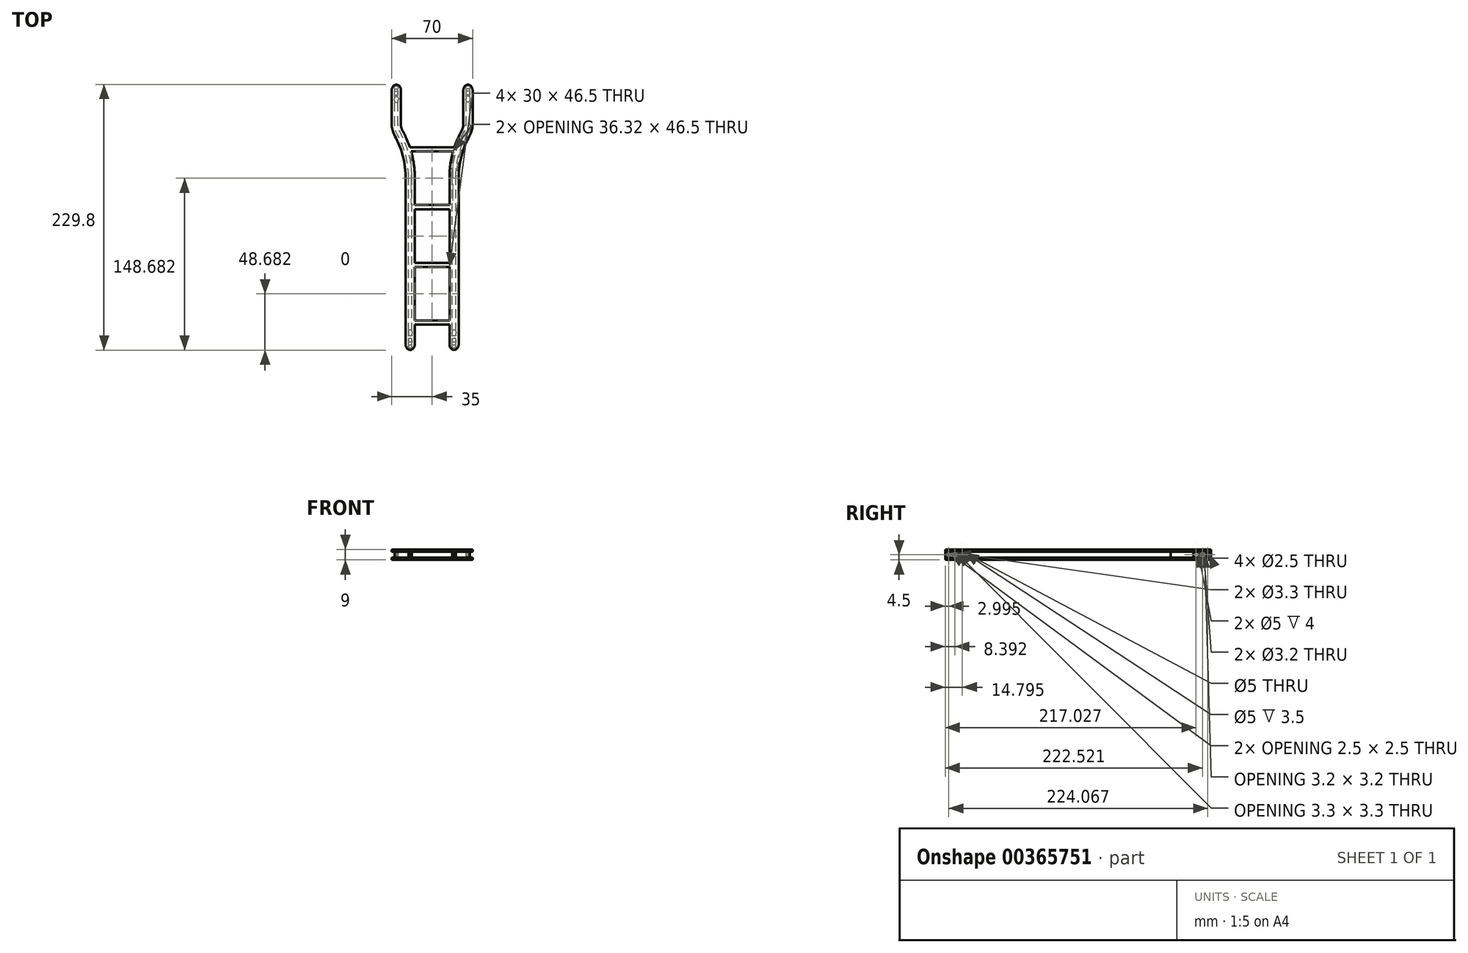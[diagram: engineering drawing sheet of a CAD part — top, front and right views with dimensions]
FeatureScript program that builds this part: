
annotation { "Feature Type Name" : "Feature", "Feature Type Description" : "" }
export const myFeature = defineFeature(function(context is Context, id is Id, definition is map)
    precondition{}
    {
        {
            var Q0;
            Q0=qCreatedBy(makeId("Front.planeOp"),FACE);
            var sketch = newSketch(context, id + "F0", { "sketchPlane" : qUnion([Q0])});
            skLineSegment(sketch, "E0.bottom", {"start": v(-15, 0) * mm, "end": v(-23, 0) * mm});
            skLineSegment(sketch, "E0.top", {"start": v(-15, 9) * mm, "end": v(-23, 9) * mm});
            skLineSegment(sketch, "E0.left", {"start": v(-15, 0) * mm, "end": v(-15, 2) * mm});
            skLineSegment(sketch, "E0.right", {"start": v(-23, 0) * mm, "end": v(-23, 2) * mm});
            skLineSegment(sketch, "E1.bottom", {"start": v(-23, 7) * mm, "end": v(-21, 7) * mm});
            skLineSegment(sketch, "E1.top", {"start": v(-23, 2) * mm, "end": v(-21, 2) * mm});
            skLineSegment(sketch, "E1.right", {"start": v(-20.5, 6.5) * mm, "end": v(-20.5, 2.5) * mm});
            skLineSegment(sketch, "E2.bottom", {"start": v(-17, 7) * mm, "end": v(-15, 7) * mm});
            skLineSegment(sketch, "E2.top", {"start": v(-17, 2) * mm, "end": v(-15, 2) * mm});
            skLineSegment(sketch, "E2.left", {"start": v(-17.5, 6.5) * mm, "end": v(-17.5, 2.5) * mm});
            skLineSegment(sketch, "E3", {"start": v(-19, 9) * mm, "end": v(-19, -4.59) * mm, "construction": true});
            skPoint(sketch, "E3.endSnap0", {"position": v(-19, 0) * mm});
            skLineSegment(sketch, "E4.trimOffspring", {"start": v(-15, 7) * mm, "end": v(-15, 9) * mm});
            skLineSegment(sketch, "E5.trimOffspring", {"start": v(-23, 7) * mm, "end": v(-23, 9) * mm});
            skPoint(sketch, "E6.visualSharp", {"position": v(-20.5, 7) * mm});
            skArc(sketch, "E6.filletArc", {"start": v(-20.5, 6.5) * mm, "mid": v(-20.65, 6.85) * mm, "end": v(-21, 7) * mm});
            skPoint(sketch, "E7.visualSharp", {"position": v(-17.5, 7) * mm});
            skArc(sketch, "E7.filletArc", {"start": v(-17, 7) * mm, "mid": v(-17.35, 6.85) * mm, "end": v(-17.5, 6.5) * mm});
            skPoint(sketch, "E8.visualSharp", {"position": v(-17.5, 2) * mm});
            skArc(sketch, "E8.filletArc", {"start": v(-17.5, 2.5) * mm, "mid": v(-17.35, 2.15) * mm, "end": v(-17, 2) * mm});
            skPoint(sketch, "E9.visualSharp", {"position": v(-20.5, 2) * mm});
            skArc(sketch, "E9.filletArc", {"start": v(-21, 2) * mm, "mid": v(-20.65, 2.15) * mm, "end": v(-20.5, 2.5) * mm});
            skSolve(sketch);
        }
        {
            var Q0;
            Q0=qCreatedBy(makeId("Top.planeOp"),FACE);
            var sketch = newSketch(context, id + "F1", { "sketchPlane" : qUnion([Q0])});
            skLineSegment(sketch, "E10", {"start": v(-35.26, 0) * mm, "end": v(-35.26, 150) * mm});
            skLineSegment(sketch, "E11", {"start": v(-47.26, 230) * mm, "end": v(-47.26, 195) * mm});
            skFitSpline(sketch, "E12", {"points": [v(-35.26, 150) * mm, v(-40.7, 174.86) * mm, v(-47.26, 195) * mm], "startDerivative": vector(-0.38, 53.31) * mm, "endDerivative": vector(-0.87, 58.08) * mm});
            skSolve(sketch);
        }
        {
            var Q0;
            Q0 = qSketchRegion(id + "F0", true);
            var Q1;
            Q1 = qConstructionFilter(qBodyType(qCreatedBy(id + "F1" ,EDGE), BodyType.WIRE), ConstructionObject.NO);
            sweep(context, id + "F2", {"profiles" : qUnion([Q0]), "path" : qUnion([Q1])});
        }
        {
            var Q0;
            Q0=makeQuery(id+"F2.opSweep","SWEPT_FACE",FACE,{"disambiguationData":[OSD([sQuery(id+"F0.wireOp",EDGE,"E4.trimOffspring"),sQuery(id+"F1.wireOp",EDGE,"E10")])]});
            var sketch = newSketch(context, id + "F3", { "sketchPlane" : qUnion([Q0])});
            skLineSegment(sketch, "E13.bottom", {"start": v(22.03, 9) * mm, "end": v(25.53, 9) * mm});
            skLineSegment(sketch, "E13.top", {"start": v(22.03, 7) * mm, "end": v(25.53, 7) * mm});
            skLineSegment(sketch, "E13.left", {"start": v(22.03, 9) * mm, "end": v(22.03, 7) * mm});
            skLineSegment(sketch, "E13.right", {"start": v(25.53, 9) * mm, "end": v(25.53, 7) * mm});
            skLineSegment(sketch, "E14.0.1.0", {"start": v(22.03, 2) * mm, "end": v(22.03, 0) * mm});
            skLineSegment(sketch, "E14.0.1.1", {"start": v(22.03, 0) * mm, "end": v(25.53, 0) * mm});
            skLineSegment(sketch, "E14.0.1.2", {"start": v(22.03, 2) * mm, "end": v(25.53, 2) * mm});
            skLineSegment(sketch, "E14.0.1.3", {"start": v(25.53, 2) * mm, "end": v(25.53, 0) * mm});
            skLineSegment(sketch, "E14.1.0.0", {"start": v(72.03, 9) * mm, "end": v(72.03, 7) * mm});
            skLineSegment(sketch, "E14.1.0.1", {"start": v(72.03, 7) * mm, "end": v(75.53, 7) * mm});
            skLineSegment(sketch, "E14.1.0.2", {"start": v(72.03, 9) * mm, "end": v(75.53, 9) * mm});
            skLineSegment(sketch, "E14.1.0.3", {"start": v(75.53, 9) * mm, "end": v(75.53, 7) * mm});
            skLineSegment(sketch, "E14.1.1.0", {"start": v(72.03, 2) * mm, "end": v(72.03, 0) * mm});
            skLineSegment(sketch, "E14.1.1.1", {"start": v(72.03, 0) * mm, "end": v(75.53, 0) * mm});
            skLineSegment(sketch, "E14.1.1.2", {"start": v(72.03, 2) * mm, "end": v(75.53, 2) * mm});
            skLineSegment(sketch, "E14.1.1.3", {"start": v(75.53, 2) * mm, "end": v(75.53, 0) * mm});
            skLineSegment(sketch, "E14.2.0.0", {"start": v(122.03, 9) * mm, "end": v(122.03, 7) * mm});
            skLineSegment(sketch, "E14.2.0.1", {"start": v(122.03, 7) * mm, "end": v(125.53, 7) * mm});
            skLineSegment(sketch, "E14.2.0.2", {"start": v(122.03, 9) * mm, "end": v(125.53, 9) * mm});
            skLineSegment(sketch, "E14.2.0.3", {"start": v(125.53, 9) * mm, "end": v(125.53, 7) * mm});
            skLineSegment(sketch, "E14.2.1.0", {"start": v(122.03, 2) * mm, "end": v(122.03, 0) * mm});
            skLineSegment(sketch, "E14.2.1.1", {"start": v(122.03, 0) * mm, "end": v(125.53, 0) * mm});
            skLineSegment(sketch, "E14.2.1.2", {"start": v(122.03, 2) * mm, "end": v(125.53, 2) * mm});
            skLineSegment(sketch, "E14.2.1.3", {"start": v(125.53, 2) * mm, "end": v(125.53, 0) * mm});
            skLineSegment(sketch, "E14.3.0.0", {"start": v(172.03, 9) * mm, "end": v(172.03, 7) * mm});
            skLineSegment(sketch, "E14.3.0.1", {"start": v(172.03, 7) * mm, "end": v(175.53, 7) * mm});
            skLineSegment(sketch, "E14.3.0.2", {"start": v(172.03, 9) * mm, "end": v(175.53, 9) * mm});
            skLineSegment(sketch, "E14.3.0.3", {"start": v(175.53, 9) * mm, "end": v(175.53, 7) * mm});
            skLineSegment(sketch, "E14.3.1.0", {"start": v(172.03, 2) * mm, "end": v(172.03, 0) * mm});
            skLineSegment(sketch, "E14.3.1.1", {"start": v(172.03, 0) * mm, "end": v(175.53, 0) * mm});
            skLineSegment(sketch, "E14.3.1.2", {"start": v(172.03, 2) * mm, "end": v(175.53, 2) * mm});
            skLineSegment(sketch, "E14.3.1.3", {"start": v(175.53, 2) * mm, "end": v(175.53, 0) * mm});
            skLineSegment(sketch, "E14.direction1", {"start": v(22.03, 7) * mm, "end": v(72.03, 7) * mm, "construction": true});
            skLineSegment(sketch, "E14.direction2", {"start": v(22.03, 7) * mm, "end": v(22.03, 0) * mm, "construction": true});
            skSolve(sketch);
        }
        {
            var Q0;
            Q0 = qSketchRegion(id + "F3", true);
            extrude(context, id + "F4", {"entities" : qUnion([Q0]), "operationType" : NewBodyOperationType.ADD, "depth" : 15 * mm});
        }
        {
            var Q0;
            Q0=makeQuery(id+"F4.opExtrude","CAP_FACE",FACE,{"disambiguationData":[OSD([sQuery(id+"F3.wireOp",EDGE,"E14.3.0.0"),sQuery(id+"F3.wireOp",EDGE,"E14.3.0.1"),sQuery(id+"F3.wireOp",EDGE,"E14.3.0.2"),sQuery(id+"F3.wireOp",EDGE,"E14.3.0.3")])],"isStart":true});
            var sketch = newSketch(context, id + "F5", { "sketchPlane" : qUnion([Q0])});
            skLineSegment(sketch, "E15.0", {"start": v(-172.03, 7) * mm, "end": v(-175.53, 7) * mm});
            skLineSegment(sketch, "E16.0.0", {"start": v(-175.53, 9) * mm, "end": v(-175.53, 7) * mm});
            skLineSegment(sketch, "E16.0.1", {"start": v(-175.53, 7) * mm, "end": v(-172.03, 7) * mm});
            skLineSegment(sketch, "E16.0.2", {"start": v(-172.03, 7) * mm, "end": v(-172.03, 9) * mm});
            skLineSegment(sketch, "E16.0.3", {"start": v(-172.03, 9) * mm, "end": v(-175.53, 9) * mm});
            skLineSegment(sketch, "E17.0.0", {"start": v(-175.53, 2) * mm, "end": v(-175.53, 0) * mm});
            skLineSegment(sketch, "E17.0.1", {"start": v(-175.53, 0) * mm, "end": v(-172.03, 0) * mm});
            skLineSegment(sketch, "E17.0.2", {"start": v(-172.03, 0) * mm, "end": v(-172.03, 2) * mm});
            skLineSegment(sketch, "E17.0.3", {"start": v(-172.03, 2) * mm, "end": v(-175.53, 2) * mm});
            skSolve(sketch);
        }
        {
            var Q0;
            Q0 = qSketchRegion(id + "F5", true);
            extrude(context, id + "F6", {"entities" : qUnion([Q0]), "operationType" : NewBodyOperationType.ADD, "endBound" : BoundingType.UP_TO_NEXT, "depth" : 25 * mm});
        }
        {
            var Q0;
            Q0=makeQuery(id+"F2.opSweep","SWEPT_BODY",BODY,{"disambiguationData":[OSD([sQuery(id+"F0.wireOp",EDGE,"E0.bottom"),sQuery(id+"F0.wireOp",EDGE,"E0.top"),sQuery(id+"F0.wireOp",EDGE,"E0.left"),sQuery(id+"F0.wireOp",EDGE,"E0.right"),sQuery(id+"F0.wireOp",EDGE,"E1.bottom"),sQuery(id+"F0.wireOp",EDGE,"E1.top"),sQuery(id+"F0.wireOp",EDGE,"E1.right"),sQuery(id+"F0.wireOp",EDGE,"E2.bottom"),sQuery(id+"F0.wireOp",EDGE,"E2.top"),sQuery(id+"F0.wireOp",EDGE,"E2.left"),sQuery(id+"F0.wireOp",EDGE,"E4.trimOffspring"),sQuery(id+"F0.wireOp",EDGE,"E5.trimOffspring"),sQuery(id+"F0.wireOp",EDGE,"E6.filletArc"),sQuery(id+"F0.wireOp",EDGE,"E7.filletArc"),sQuery(id+"F0.wireOp",EDGE,"E8.filletArc"),sQuery(id+"F0.wireOp",EDGE,"E9.filletArc"),sQuery(id+"F1.wireOp",EDGE,"E11")])]});
            var Q1;
            Q1=makeQuery(id+"F4.opExtrude","CAP_FACE",FACE,{"disambiguationData":[OSD([sQuery(id+"F3.wireOp",EDGE,"E14.1.0.0"),sQuery(id+"F3.wireOp",EDGE,"E14.1.0.1"),sQuery(id+"F3.wireOp",EDGE,"E14.1.0.2"),sQuery(id+"F3.wireOp",EDGE,"E14.1.0.3")])],"isStart":false});
            mirror(context, id + "F7", {"operationType" : NewBodyOperationType.ADD, "entities" : qUnion([Q0]), "mirrorPlane" : qUnion([Q1])});
        }
        {
            var Q0;
            Q0=makeQuery(id+"F2.opSweep","SWEPT_FACE",FACE,{"disambiguationData":[OSD([sQuery(id+"F0.wireOp",EDGE,"E1.right"),sQuery(id+"F1.wireOp",EDGE,"E10")])]});
            var sketch = newSketch(context, id + "F8", { "sketchPlane" : qUnion([Q0])});
            skCircle(sketch, "E18", {"center": v(-14.9, 4.5) * mm, "radius": 2.5 * mm});
            skPoint(sketch, "E18.centerSnap0", {"position": v(0, 4.5) * mm});
            skCircle(sketch, "E19", {"center": v(-3.1, 4.5) * mm, "radius": 1.25 * mm});
            skCircle(sketch, "E20", {"center": v(-8.5, 4.5) * mm, "radius": 1.65 * mm});
            skLineSegment(sketch, "E21", {"start": v(-230, 4.5) * mm, "end": v(-219.48, 4.5) * mm, "construction": true});
            skCircle(sketch, "E22", {"center": v(-227.16, 4.5) * mm, "radius": 1.25 * mm});
            skCircle(sketch, "E23", {"center": v(-222.62, 4.5) * mm, "radius": 1.6 * mm});
            skCircle(sketch, "E24", {"center": v(-217.13, 4.5) * mm, "radius": 2.5 * mm});
            skSolve(sketch);
        }
        {
            var Q0;
            Q0 = qSketchRegion(id + "F8", true);
            extrude(context, id + "F9", {"entities" : qUnion([Q0]), "operationType" : NewBodyOperationType.REMOVE, "endBound" : BoundingType.THROUGH_ALL, "oppositeDirection" : true, "depth" : 25 * mm});
        }
        {
            var Q0;
            {var subQ0=sQuery(id+"F1.wireOp",EDGE,"E11");var subQ3=sQuery(id+"F1.wireOp",EDGE,"E12");var subQ4=sQuery(id+"F0.wireOp",EDGE,"E1.right");Q0=makeQuery(id+"F9.boolean.opBoolean","SPLIT",FACE,{"disambiguationData":[TD([makeQuery(id+"F7.opPattern","COPY",FACE,{"derivedFrom":makeQuery(id+"F2.opSweep","SWEPT_FACE",FACE,{"disambiguationData":[OSD([subQ4,subQ3])]}),"instanceName":"1"})])],"derivedFrom":makeQuery(id+"F7.opPattern","COPY",FACE,{"derivedFrom":makeQuery(id+"F2.opSweep","SWEPT_FACE",FACE,{"disambiguationData":[OSD([subQ4,subQ0])]}),"instanceName":"1"})});}
            var sketch = newSketch(context, id + "F10", { "sketchPlane" : qUnion([Q0])});
            skArc(sketch, "E25.0", {"start": v(218.63, 2.5) * mm, "mid": v(219.63, 4.5) * mm, "end": v(218.63, 6.5) * mm});
            skArc(sketch, "E26.0", {"start": v(215.63, 6.5) * mm, "mid": v(214.63, 4.5) * mm, "end": v(215.63, 2.5) * mm});
            skArc(sketch, "E27.0", {"start": v(215.63, 6.5) * mm, "mid": v(216.34, 6.87) * mm, "end": v(217.13, 7) * mm});
            skArc(sketch, "E28.0", {"start": v(217.13, 7) * mm, "mid": v(217.92, 6.87) * mm, "end": v(218.63, 6.5) * mm});
            skArc(sketch, "E29.0", {"start": v(217.13, 2) * mm, "mid": v(216.34, 2.13) * mm, "end": v(215.63, 2.5) * mm});
            skArc(sketch, "E30.0", {"start": v(218.63, 2.5) * mm, "mid": v(217.92, 2.13) * mm, "end": v(217.13, 2) * mm});
            skCircle(sketch, "E31.0", {"center": v(222.62, 4.5) * mm, "radius": 1.6 * mm});
            skCircle(sketch, "E32.0", {"center": v(227.16, 4.5) * mm, "radius": 1.25 * mm});
            skSolve(sketch);
        }
        {
            var Q0;
            Q0 = qSketchRegion(id + "F10", true);
            extrude(context, id + "F11", {"entities" : qUnion([Q0]), "operationType" : NewBodyOperationType.REMOVE, "endBound" : BoundingType.THROUGH_ALL, "oppositeDirection" : true, "depth" : 25 * mm});
        }
        {
            var Q0;
            Q0=makeQuery(id+"F7.opPattern","COPY",EDGE,{"derivedFrom":makeQuery(id+"F2.opSweep","CAP_EDGE",EDGE,{"disambiguationData":[OSD([sQuery(id+"F0.wireOp",EDGE,"E5.trimOffspring"),sQuery(id+"F1.wireOp",VERTEX,"E11.start")])],"isStart":false}),"instanceName":"1"});
            var Q1;
            Q1=makeQuery(id+"F7.opPattern","COPY",EDGE,{"derivedFrom":makeQuery(id+"F2.opSweep","CAP_EDGE",EDGE,{"disambiguationData":[OSD([sQuery(id+"F0.wireOp",EDGE,"E4.trimOffspring"),sQuery(id+"F1.wireOp",VERTEX,"E11.start")])],"isStart":false}),"instanceName":"1"});
            var Q2;
            Q2=makeQuery(id+"F2.opSweep","CAP_EDGE",EDGE,{"disambiguationData":[OSD([sQuery(id+"F0.wireOp",EDGE,"E4.trimOffspring"),sQuery(id+"F1.wireOp",VERTEX,"E11.start")])],"isStart":false});
            var Q3;
            Q3=makeQuery(id+"F2.opSweep","CAP_EDGE",EDGE,{"disambiguationData":[OSD([sQuery(id+"F0.wireOp",EDGE,"E5.trimOffspring"),sQuery(id+"F1.wireOp",VERTEX,"E11.start")])],"isStart":false});
            var Q4;
            Q4=makeQuery(id+"F2.opSweep","CAP_EDGE",EDGE,{"disambiguationData":[OSD([sQuery(id+"F0.wireOp",EDGE,"E4.trimOffspring"),sQuery(id+"F1.wireOp",VERTEX,"E10.start")])],"isStart":true});
            var Q5;
            Q5=makeQuery(id+"F2.opSweep","CAP_EDGE",EDGE,{"disambiguationData":[OSD([sQuery(id+"F0.wireOp",EDGE,"E5.trimOffspring"),sQuery(id+"F1.wireOp",VERTEX,"E10.start")])],"isStart":true});
            var Q6;
            Q6=makeQuery(id+"F7.opPattern","COPY",EDGE,{"derivedFrom":makeQuery(id+"F2.opSweep","CAP_EDGE",EDGE,{"disambiguationData":[OSD([sQuery(id+"F0.wireOp",EDGE,"E5.trimOffspring"),sQuery(id+"F1.wireOp",VERTEX,"E10.start")])],"isStart":true}),"instanceName":"1"});
            var Q7;
            Q7=makeQuery(id+"F7.opPattern","COPY",EDGE,{"derivedFrom":makeQuery(id+"F2.opSweep","CAP_EDGE",EDGE,{"disambiguationData":[OSD([sQuery(id+"F0.wireOp",EDGE,"E4.trimOffspring"),sQuery(id+"F1.wireOp",VERTEX,"E10.start")])],"isStart":true}),"instanceName":"1"});
            fillet(context, id + "F12", {"entities" : qUnion([Q0, Q1, Q2, Q3, Q4, Q5, Q6, Q7]), "radius" : 5 * mm, "tangentPropagation" : true, "allowEdgeOverflow" : false});
        }
    });
